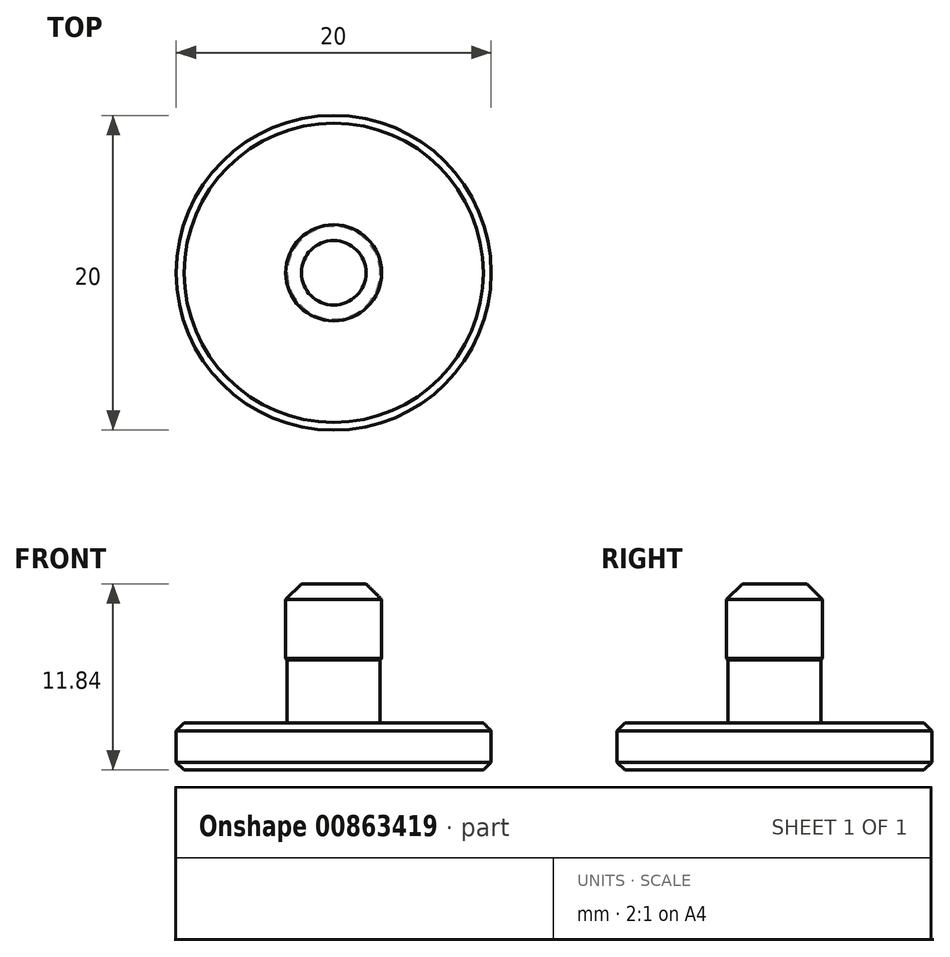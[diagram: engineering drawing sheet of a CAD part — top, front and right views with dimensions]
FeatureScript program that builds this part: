
annotation { "Feature Type Name" : "Feature", "Feature Type Description" : "" }
export const myFeature = defineFeature(function(context is Context, id is Id, definition is map)
    precondition{}
    {
        {
            var Q0;
            Q0=qCreatedBy(makeId("Top.planeOp"),FACE);
            var sketch = newSketch(context, id + "F0", { "sketchPlane" : qUnion([Q0])});
            skCircle(sketch, "E0", {"center": v(0, 0) * mm, "radius": 10 * mm});
            skSolve(sketch);
        }
        {
            var Q0;
            Q0=makeQuery(id+"F0.imprint","IMPRINT",FACE,{"disambiguationData":[TD([[makeQuery(id+"F0.imprint","IMPRINT",EDGE,{"derivedFrom":sQuery(id+"F0.wireOp",EDGE,"E0")}),1.0]])]});
            extrude(context, id + "F1", {"entities" : qUnion([Q0]), "depth" : 3 * mm, "offsetDistance" : 25 * mm});
        }
        {
            var Q0;
            Q0=makeQuery(id+"F1.opExtrude","CAP_FACE",FACE,{"disambiguationData":[OSD([sQuery(id+"F0.wireOp",EDGE,"E0")])],"isStart":false});
            var sketch = newSketch(context, id + "F2", { "sketchPlane" : qUnion([Q0])});
            skCircle(sketch, "E1", {"center": v(0, 0) * mm, "radius": 2.95 * mm});
            skSolve(sketch);
        }
        {
            var Q0;
            Q0=makeQuery(id+"F2.imprint","IMPRINT",FACE,{"disambiguationData":[TD([[makeQuery(id+"F2.imprint","IMPRINT",EDGE,{"derivedFrom":sQuery(id+"F2.wireOp",EDGE,"E1")}),1.0]])]});
            extrude(context, id + "F3", {"entities" : qUnion([Q0]), "operationType" : NewBodyOperationType.ADD, "depth" : 3.6 * mm, "offsetDistance" : 25 * mm});
        }
        {
            var Q0;
            Q0=makeQuery(id+"F3.opExtrude","CAP_FACE",FACE,{"disambiguationData":[OSD([sQuery(id+"F2.wireOp",EDGE,"E1")])],"isStart":false});
            var sketch = newSketch(context, id + "F4", { "sketchPlane" : qUnion([Q0])});
            skCircle(sketch, "E2", {"center": v(0, 0) * mm, "radius": 3.05 * mm});
            skSolve(sketch);
        }
        {
            var Q0;
            Q0=makeQuery(id+"F4.imprint","IMPRINT",FACE,{"disambiguationData":[TD([[makeQuery(id+"F4.imprint","IMPRINT",EDGE,{"derivedFrom":sQuery(id+"F4.wireOp",EDGE,"E2")}),1.0]])]});
            var Q1;
            Q1=makeQuery(id+"F4.imprint","IMPRINT",FACE,{"disambiguationData":[TD([[makeQuery(id+"F4.imprint","IMPRINT",EDGE,{"derivedFrom":makeQuery(id+"F3.opExtrude","CAP_EDGE",EDGE,{"disambiguationData":[OSD([sQuery(id+"F2.wireOp",EDGE,"E1")])],"isStart":false})}),1.0]])]});
            extrude(context, id + "F5", {"entities" : qUnion([Q0, Q1]), "operationType" : NewBodyOperationType.ADD, "depth" : 5.23 * mm, "offsetDistance" : 25 * mm});
        }
        {
            var Q0;
            Q0=makeQuery(id+"F5.opExtrude","CAP_EDGE",EDGE,{"disambiguationData":[OSD([sQuery(id+"F4.wireOp",EDGE,"E2")])],"isStart":false});
            chamfer(context, id + "F6", {"entities" : qUnion([Q0]), "width" : 1 * mm, "tangentPropagation" : true});
        }
        {
            var Q0;
            Q0=makeQuery(id+"F1.opExtrude","CAP_EDGE",EDGE,{"disambiguationData":[OSD([sQuery(id+"F0.wireOp",EDGE,"E0")])],"isStart":false});
            var Q1;
            Q1=makeQuery(id+"F1.opExtrude","CAP_EDGE",EDGE,{"disambiguationData":[OSD([sQuery(id+"F0.wireOp",EDGE,"E0")])],"isStart":true});
            chamfer(context, id + "F7", {"entities" : qUnion([Q0, Q1]), "width" : .5 * mm, "tangentPropagation" : true});
        }
        {
            var Q0;
            Q0=makeQuery(id+"F5.opExtrude","CAP_EDGE",EDGE,{"disambiguationData":[OSD([sQuery(id+"F4.wireOp",EDGE,"E2")])],"isStart":true});
            chamfer(context, id + "F8", {"entities" : qUnion([Q0]), "width" : .5 * mm, "tangentPropagation" : true});
        }
    });
